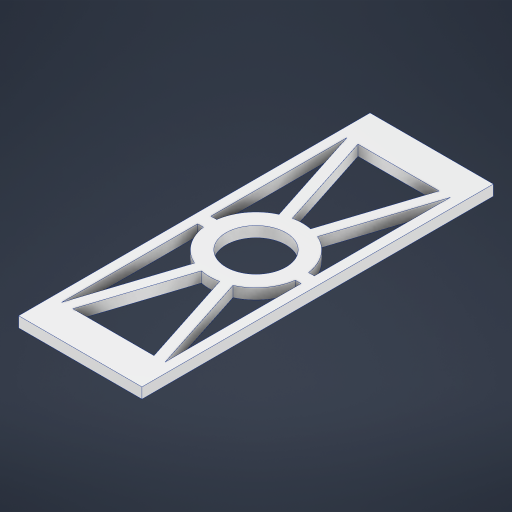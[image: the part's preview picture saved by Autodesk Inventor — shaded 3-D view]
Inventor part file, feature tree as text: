
AUTODESK INVENTOR PART (.ipt)
format: ipt  version: 2024 (Build 280153000, 153)  size: 315,904 bytes
history: native  units: mm
features: extrude x6, sketch x6, projected_geometry x1
ambient origin geometry x8: Origin, YZ Plane, XZ Plane, XY Plane, X Axis, Y Axis, Z Axis, Center Point
bodies: Solid1 (feature_tree)
feature tree (13):
  extrude  "Extrusion1"  Depth=186.0mm
  extrude  "Extrusion2"  Depth=16.0mm TaperAngle=0.0deg
  extrude  "Extrusion3"  Depth=25.0mm
  extrude  "Extrusion4"  Depth=50.0mm
  extrude  "Extrusion5"  Depth=15.0mm
  extrude  "Extrusion6"  Depth=20.0mm TaperAngle=0.0deg
  sketch  "Sketch1"  dims[d0=542.0mm d1=186.0mm]
  sketch  "Sketch2"  dims[d2=90.0mm d3=16.0mm d4=0.0mm]
  sketch  "Sketch3"  dims[d5=6.0mm d6=25.0mm]
  projected_geometry  "Projected Loop1"
  sketch  "Sketch4"  dims[d7=25.0mm d8=50.0mm]
  sketch  "Sketch5"  dims[d9=15.0mm d10=15.0mm]
  sketch  "Sketch6"  dims[d11=50.0mm d12=20.0mm d13=0.0mm d14=25.0mm d15=15.0mm d16=10.0mm d17=10.0mm d18=8.0mm d19=8.0mm d20=8.0mm d21=8.0mm d22=20.0mm d23=0.0mm d24=16.0mm d25=0.0mm d26=40.0mm d27=40.0mm d28=100.0mm d29=0.0mm d30=10.0mm d31=0.0mm d32=10.0mm d33=10.0mm d34=0.0mm]
